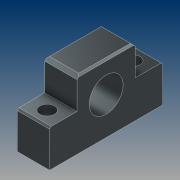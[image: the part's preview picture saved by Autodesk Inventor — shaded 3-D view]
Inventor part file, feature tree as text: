
AUTODESK INVENTOR PART (.ipt)
format: ipt  version: 2021 (Build 250183000, 183)  size: 137,216 bytes
history: native  units: mm
features: chamfer x3, sketch x2, projected_geometry x2, extrude x1, hole x1
ambient origin geometry x8: Origin, YZ Plane, XZ Plane, XY Plane, X Axis, Y Axis, Z Axis, Center Point
bodies: Solid1 (feature_tree)
feature tree (9):
  extrude  "Extrusion1"  Depth=70.0mm
  hole  "Hole1"  [1 undecoded]
  chamfer  "Chamfer1"  Distance=21.0mm
  chamfer  "Chamfer2"  Distance=20.0mm
  chamfer  "Chamfer3"  Distance=1.0mm Angle=45.0deg
  sketch  "Sketch1"  dims[d0=36.0mm d1=70.0mm]
  sketch  "Sketch2"  dims[d2=19.0mm d3=24.0mm d4=21.0mm d5=20.0mm d6=0.0mm d7=9.0mm d8=6.0mm d9=4.0mm d10=2.0mm d11=90.0deg d12=8.0mm d13=20.594885mm d14=1.0mm d15=2.0mm d16=45.0deg d17=1.0mm d18=2.0mm d19=45.0deg d20=2.0mm d21=2.0mm d22=45.0deg]
  projected_geometry  "Projected Loop1"
  projected_geometry  "Projected Loop2"
note: 1 required parameter value undecoded (feature->parameter linkage not recoverable at this tier; creation-order binding heuristic only, values carry confidence <= 0.55)
